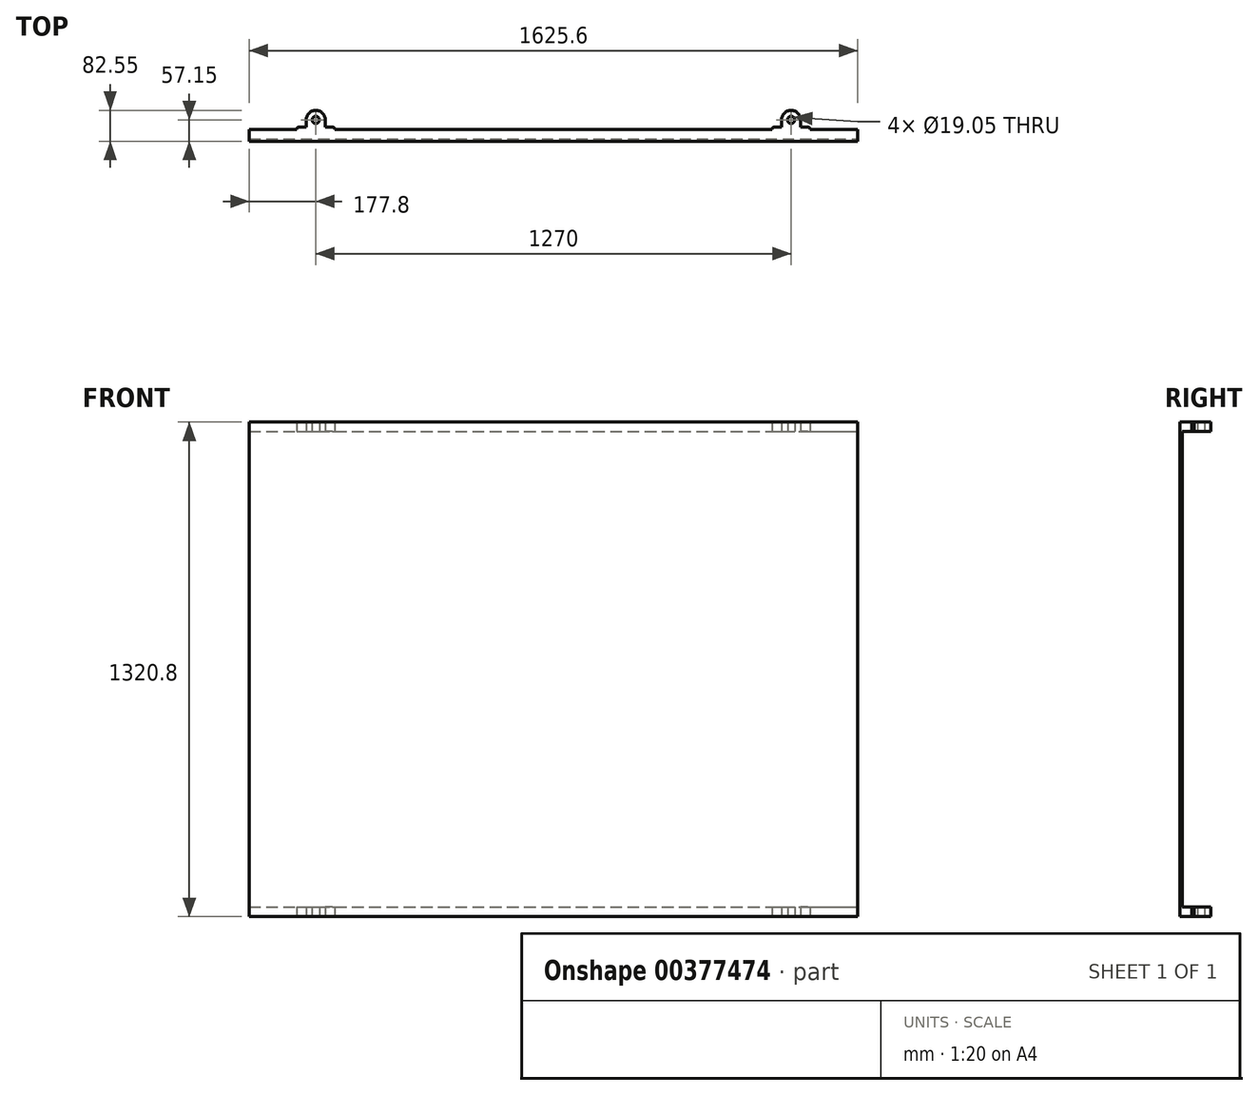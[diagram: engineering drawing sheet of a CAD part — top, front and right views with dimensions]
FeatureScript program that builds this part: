
annotation { "Feature Type Name" : "Feature", "Feature Type Description" : "" }
export const myFeature = defineFeature(function(context is Context, id is Id, definition is map)
    precondition{}
    {
        {
            var Q0;
            Q0=qCreatedBy(makeId("Front.planeOp"),FACE);
            var sketch = newSketch(context, id + "F0", { "sketchPlane" : qUnion([Q0])});
            skLineSegment(sketch, "E0.bottom", {"start": v(-25.4, 961.2) * mm, "end": v(1600.2, 961.2) * mm});
            skLineSegment(sketch, "E0.top", {"start": v(-25.4, 935.8) * mm, "end": v(1600.2, 935.8) * mm});
            skLineSegment(sketch, "E0.left", {"start": v(-25.4, 961.2) * mm, "end": v(-25.4, 935.8) * mm});
            skLineSegment(sketch, "E0.right", {"start": v(1600.2, 961.2) * mm, "end": v(1600.2, 935.8) * mm});
            skPoint(sketch, "E1.firstSnap0", {"position": v(787.4, 961.2) * mm});
            skLineSegment(sketch, "E2.bottom", {"start": v(-25.4, 935.8) * mm, "end": v(0, 935.8) * mm});
            skLineSegment(sketch, "E2.top", {"start": v(-25.4, -334.2) * mm, "end": v(0, -334.2) * mm});
            skLineSegment(sketch, "E2.left", {"start": v(-25.4, 935.8) * mm, "end": v(-25.4, -334.2) * mm});
            skLineSegment(sketch, "E2.right", {"start": v(0, 935.8) * mm, "end": v(0, -334.2) * mm});
            skLineSegment(sketch, "E3.bottom", {"start": v(-25.4, -334.2) * mm, "end": v(1600.2, -334.2) * mm});
            skLineSegment(sketch, "E3.top", {"start": v(-25.4, -359.6) * mm, "end": v(1600.2, -359.6) * mm});
            skLineSegment(sketch, "E3.left", {"start": v(-25.4, -334.2) * mm, "end": v(-25.4, -359.6) * mm});
            skLineSegment(sketch, "E3.right", {"start": v(1600.2, -334.2) * mm, "end": v(1600.2, -359.6) * mm});
            skLineSegment(sketch, "E4.bottom", {"start": v(1600.2, 935.8) * mm, "end": v(1574.8, 935.8) * mm});
            skLineSegment(sketch, "E4.top", {"start": v(1600.2, -334.2) * mm, "end": v(1574.8, -334.2) * mm});
            skLineSegment(sketch, "E4.left", {"start": v(1600.2, 935.8) * mm, "end": v(1600.2, -334.2) * mm});
            skLineSegment(sketch, "E4.right", {"start": v(1574.8, 935.8) * mm, "end": v(1574.8, -334.2) * mm});
            skLineSegment(sketch, "E5.bottom", {"start": v(774.7, 935.8) * mm, "end": v(800.1, 935.8) * mm});
            skLineSegment(sketch, "E5.top", {"start": v(774.7, -334.2) * mm, "end": v(800.1, -334.2) * mm});
            skLineSegment(sketch, "E5.left", {"start": v(774.7, 935.8) * mm, "end": v(774.7, -334.2) * mm});
            skLineSegment(sketch, "E5.right", {"start": v(800.1, 935.8) * mm, "end": v(800.1, -334.2) * mm});
            skSolve(sketch);
        }
        {
            var Q0;
            Q0=makeQuery(id+"F0.imprint","IMPRINT",FACE,{"disambiguationData":[TD([[makeQuery(id+"F0.imprint","IMPRINT",EDGE,{"derivedFrom":sQuery(id+"F0.wireOp",EDGE,"E5.bottom")}),-1.0]])]});
            var Q1;
            Q1=makeQuery(id+"F0.imprint","IMPRINT",FACE,{"disambiguationData":[TD([[makeQuery(id+"F0.imprint","IMPRINT",EDGE,{"derivedFrom":sQuery(id+"F0.wireOp",EDGE,"E0.bottom")}),-1.0]])]});
            var Q2;
            Q2=makeQuery(id+"F0.imprint","IMPRINT",FACE,{"disambiguationData":[TD([[makeQuery(id+"F0.imprint","IMPRINT",EDGE,{"derivedFrom":sQuery(id+"F0.wireOp",EDGE,"E2.bottom")}),-1.0]])]});
            var Q3;
            Q3=makeQuery(id+"F0.imprint","IMPRINT",FACE,{"disambiguationData":[TD([[makeQuery(id+"F0.imprint","IMPRINT",EDGE,{"derivedFrom":sQuery(id+"F0.wireOp",EDGE,"E3.top")}),1.0]])]});
            var Q4;
            Q4=makeQuery(id+"F0.imprint","IMPRINT",FACE,{"disambiguationData":[TD([[makeQuery(id+"F0.imprint","IMPRINT",EDGE,{"derivedFrom":sQuery(id+"F0.wireOp",EDGE,"E4.bottom")}),1.0]])]});
            extrude(context, id + "F1", {"entities" : qUnion([Q0, Q1, Q2, Q3, Q4]), "depth" : 25.4 * mm});
        }
        {
            var Q0;
            Q0=makeQuery(id+"F1.opExtrude","CAP_FACE",FACE,{"disambiguationData":[OSD([sQuery(id+"F0.wireOp",EDGE,"E0.bottom"),sQuery(id+"F0.wireOp",EDGE,"E0.top"),sQuery(id+"F0.wireOp",EDGE,"E0.left"),sQuery(id+"F0.wireOp",EDGE,"E0.right"),sQuery(id+"F0.wireOp",EDGE,"E2.left"),sQuery(id+"F0.wireOp",EDGE,"E2.right"),sQuery(id+"F0.wireOp",EDGE,"E3.bottom"),sQuery(id+"F0.wireOp",EDGE,"E3.top"),sQuery(id+"F0.wireOp",EDGE,"E3.left"),sQuery(id+"F0.wireOp",EDGE,"E3.right"),sQuery(id+"F0.wireOp",EDGE,"E4.left"),sQuery(id+"F0.wireOp",EDGE,"E4.right"),sQuery(id+"F0.wireOp",EDGE,"E5.left"),sQuery(id+"F0.wireOp",EDGE,"E5.right")])],"isStart":false});
            var sketch = newSketch(context, id + "F2", { "sketchPlane" : qUnion([Q0])});
            skLineSegment(sketch, "E6.bottom", {"start": v(-25.4, 961.2) * mm, "end": v(1600.2, 961.2) * mm});
            skLineSegment(sketch, "E6.top", {"start": v(-25.4, -359.6) * mm, "end": v(1600.2, -359.6) * mm});
            skLineSegment(sketch, "E6.left", {"start": v(-25.4, 961.2) * mm, "end": v(-25.4, -359.6) * mm});
            skLineSegment(sketch, "E6.right", {"start": v(1600.2, 961.2) * mm, "end": v(1600.2, -359.6) * mm});
            skSolve(sketch);
        }
        {
            var Q0;
            Q0 = qSketchRegion(id + "F2", true);
            extrude(context, id + "F3", {"entities" : qUnion([Q0]), "operationType" : NewBodyOperationType.ADD, "depth" : 6.35 * mm});
        }
        {
            var Q0;
            Q0=makeQuery(id+"F3.boolean.opBoolean","MERGE",FACE,{"derivedFrom":[makeQuery(id+"F1.opExtrude","SWEPT_FACE",FACE,{"disambiguationData":[OSD([sQuery(id+"F0.wireOp",EDGE,"E3.top")])]}),makeQuery(id+"F3.opExtrude","SWEPT_FACE",FACE,{"disambiguationData":[OSD([sQuery(id+"F2.wireOp",EDGE,"E6.top")])]})]});
            var sketch = newSketch(context, id + "F4", { "sketchPlane" : qUnion([Q0])});
            skLineSegment(sketch, "E7.bottom", {"start": v(127, 0) * mm, "end": v(177.8, 0) * mm});
            skLineSegment(sketch, "E7.top", {"start": v(152.4, -50.8) * mm, "end": v(152.4, -50.8) * mm});
            skLineSegment(sketch, "E7.left", {"start": v(127, 0) * mm, "end": v(127, -25.4) * mm});
            skLineSegment(sketch, "E7.right", {"start": v(177.8, 0) * mm, "end": v(177.8, -25.4) * mm});
            skLineSegment(sketch, "E8.bottom", {"start": v(1447.8, 0) * mm, "end": v(1397, 0) * mm});
            skLineSegment(sketch, "E8.top", {"start": v(1422.4, -50.8) * mm, "end": v(1422.4, -50.8) * mm});
            skLineSegment(sketch, "E8.left", {"start": v(1447.8, 0) * mm, "end": v(1447.8, -25.4) * mm});
            skLineSegment(sketch, "E8.right", {"start": v(1397, 0) * mm, "end": v(1397, -25.4) * mm});
            skPoint(sketch, "E9.visualSharp", {"position": v(127, -50.8) * mm});
            skArc(sketch, "E9.filletArc", {"start": v(127, -25.4) * mm, "mid": v(134.44, -43.36) * mm, "end": v(152.4, -50.8) * mm});
            skPoint(sketch, "E10.visualSharp", {"position": v(177.8, -50.8) * mm});
            skArc(sketch, "E10.filletArc", {"start": v(152.4, -50.8) * mm, "mid": v(170.36, -43.36) * mm, "end": v(177.8, -25.4) * mm});
            skCircle(sketch, "E11", {"center": v(152.4, -25.4) * mm, "radius": 9.53 * mm});
            skPoint(sketch, "E11.centerSnap0", {"position": v(152.4, -50.8) * mm});
            skLineSegment(sketch, "E12.bottom", {"start": v(127, 0) * mm, "end": v(101.6, 0) * mm});
            skLineSegment(sketch, "E12.top", {"start": v(127, -6.35) * mm, "end": v(107.95, -6.35) * mm});
            skLineSegment(sketch, "E12.left", {"start": v(127, 0) * mm, "end": v(127, -6.35) * mm});
            skLineSegment(sketch, "E12.right", {"start": v(101.6, 0) * mm, "end": v(101.6, 0) * mm});
            skPoint(sketch, "E13.visualSharp", {"position": v(101.6, -6.35) * mm});
            skArc(sketch, "E13.filletArc", {"start": v(101.6, 0) * mm, "mid": v(103.46, -4.5) * mm, "end": v(107.95, -6.35) * mm});
            skLineSegment(sketch, "E14.bottom", {"start": v(177.8, 0) * mm, "end": v(203.2, 0) * mm});
            skLineSegment(sketch, "E14.top", {"start": v(177.8, -6.35) * mm, "end": v(196.85, -6.35) * mm});
            skLineSegment(sketch, "E14.left", {"start": v(177.8, 0) * mm, "end": v(177.8, -6.35) * mm});
            skLineSegment(sketch, "E14.right", {"start": v(203.2, 0) * mm, "end": v(203.2, 0) * mm});
            skPoint(sketch, "E15.visualSharp", {"position": v(203.2, -6.35) * mm});
            skArc(sketch, "E15.filletArc", {"start": v(196.85, -6.35) * mm, "mid": v(201.34, -4.5) * mm, "end": v(203.2, 0) * mm});
            skPoint(sketch, "E16.visualSharp", {"position": v(1397, -50.8) * mm});
            skArc(sketch, "E16.filletArc", {"start": v(1397, -25.4) * mm, "mid": v(1404.44, -43.36) * mm, "end": v(1422.4, -50.8) * mm});
            skPoint(sketch, "E17.visualSharp", {"position": v(1447.8, -50.8) * mm});
            skArc(sketch, "E17.filletArc", {"start": v(1422.4, -50.8) * mm, "mid": v(1440.36, -43.36) * mm, "end": v(1447.8, -25.4) * mm});
            skCircle(sketch, "E18", {"center": v(1422.4, -25.4) * mm, "radius": 9.53 * mm});
            skLineSegment(sketch, "E19.bottom", {"start": v(1397, 0) * mm, "end": v(1371.6, 0) * mm});
            skLineSegment(sketch, "E19.top", {"start": v(1397, -6.35) * mm, "end": v(1377.95, -6.35) * mm});
            skLineSegment(sketch, "E19.left", {"start": v(1397, 0) * mm, "end": v(1397, -6.35) * mm});
            skLineSegment(sketch, "E19.right", {"start": v(1371.6, 0) * mm, "end": v(1371.6, 0) * mm});
            skLineSegment(sketch, "E20.bottom", {"start": v(1447.8, 0) * mm, "end": v(1473.2, 0) * mm});
            skLineSegment(sketch, "E20.top", {"start": v(1447.8, -6.35) * mm, "end": v(1466.85, -6.35) * mm});
            skLineSegment(sketch, "E20.left", {"start": v(1447.8, 0) * mm, "end": v(1447.8, -6.35) * mm});
            skLineSegment(sketch, "E20.right", {"start": v(1473.2, 0) * mm, "end": v(1473.2, 0) * mm});
            skPoint(sketch, "E21.visualSharp", {"position": v(1473.2, -6.35) * mm});
            skArc(sketch, "E21.filletArc", {"start": v(1466.85, -6.35) * mm, "mid": v(1471.34, -4.5) * mm, "end": v(1473.2, 0) * mm});
            skPoint(sketch, "E22.visualSharp", {"position": v(1371.6, -6.35) * mm});
            skArc(sketch, "E22.filletArc", {"start": v(1371.6, 0) * mm, "mid": v(1373.46, -4.5) * mm, "end": v(1377.95, -6.35) * mm});
            skSolve(sketch);
        }
        {
            var Q0;
            Q0 = qSketchRegion(id + "F4", true);
            extrude(context, id + "F5", {"entities" : qUnion([Q0]), "operationType" : NewBodyOperationType.ADD, "oppositeDirection" : true, "depth" : 1320.8 * mm});
        }
        {
            var Q0;
            Q0=makeQuery(id+"F3.boolean.opBoolean","MERGE",FACE,{"derivedFrom":[makeQuery(id+"F1.opExtrude","SWEPT_FACE",FACE,{"disambiguationData":[OSD([sQuery(id+"F0.wireOp",EDGE,"E0.right"),sQuery(id+"F0.wireOp",EDGE,"E3.right"),sQuery(id+"F0.wireOp",EDGE,"E4.left")])]}),makeQuery(id+"F3.opExtrude","SWEPT_FACE",FACE,{"disambiguationData":[OSD([sQuery(id+"F2.wireOp",EDGE,"E6.right")])]})]});
            var sketch = newSketch(context, id + "F6", { "sketchPlane" : qUnion([Q0])});
            skLineSegment(sketch, "E23.bottom", {"start": v(0, 935.8) * mm, "end": v(50.8, 935.8) * mm});
            skLineSegment(sketch, "E23.top", {"start": v(0, -334.2) * mm, "end": v(50.8, -334.2) * mm});
            skLineSegment(sketch, "E23.left", {"start": v(0, 935.8) * mm, "end": v(0, -334.2) * mm});
            skLineSegment(sketch, "E23.right", {"start": v(50.8, 935.8) * mm, "end": v(50.8, -334.2) * mm});
            skSolve(sketch);
        }
        {
            var Q0;
            Q0=makeQuery(id+"F6.imprint","IMPRINT",FACE,{"disambiguationData":[TD([[makeQuery(id+"F6.imprint","IMPRINT",EDGE,{"derivedFrom":sQuery(id+"F6.wireOp",EDGE,"E23.bottom")}),-1.0]])]});
            extrude(context, id + "F7", {"entities" : qUnion([Q0]), "operationType" : NewBodyOperationType.REMOVE, "endBound" : BoundingType.THROUGH_ALL, "oppositeDirection" : true, "depth" : 25.4 * mm});
        }
    });
